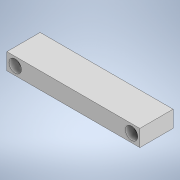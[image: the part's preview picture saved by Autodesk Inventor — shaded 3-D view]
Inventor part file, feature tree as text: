
AUTODESK INVENTOR PART (.ipt)
format: ipt  version: 2021 (Build 250183000, 183)  size: 118,784 bytes
history: native  units: in
note: dims shown in document units (in); Inventor stores cm internally (conversion verified against a paired STEP export)
features: sketch x2, extrude x1, hole x1, mirror x1, projected_geometry x1
ambient origin geometry x8: Origin, YZ Plane, XZ Plane, XY Plane, X Axis, Y Axis, Z Axis, Center Point
bodies: Solid1 (feature_tree)
feature tree (6):
  extrude  "Extrusion1"  Depth=0.5in
  hole  "Hole1"  [1 undecoded]
  mirror  "Mirror1"
  sketch  "Sketch1"  dims[d0=4.0in d1=0.5in]
  sketch  "Sketch2"  dims[d2=1.0in d3=0.0in d5=1.75in d6=0.25in d7=0.75in d8=0.375in d9=0.25in d10=0.5635in d11=0.12in d12=0.0in]
  projected_geometry  "Projected Loop1"
note: 1 required parameter value undecoded (feature->parameter linkage not recoverable at this tier; creation-order binding heuristic only, values carry confidence <= 0.55)
